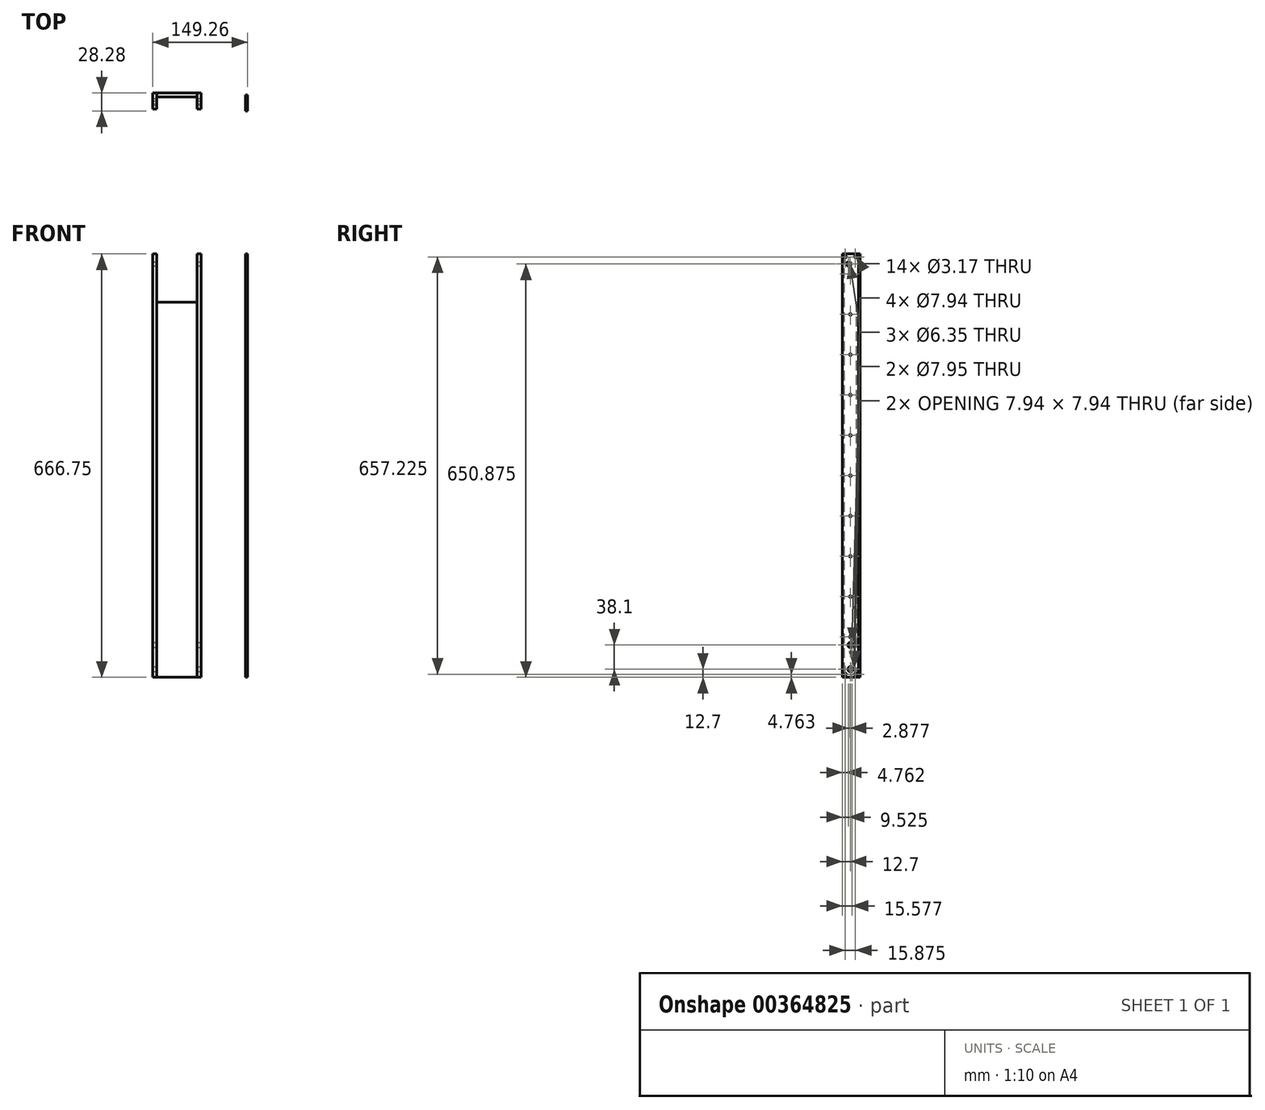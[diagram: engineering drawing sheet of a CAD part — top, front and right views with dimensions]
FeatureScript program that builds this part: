
annotation { "Feature Type Name" : "Feature", "Feature Type Description" : "" }
export const myFeature = defineFeature(function(context is Context, id is Id, definition is map)
    precondition{}
    {
        {
            var Q0;
            Q0=qCreatedBy(makeId("Top.planeOp"),FACE);
            var sketch = newSketch(context, id + "F0", { "sketchPlane" : qUnion([Q0])});
            skLineSegment(sketch, "E0", {"start": v(-38.1, -22.52) * mm, "end": v(-38.1, 2.88) * mm});
            skLineSegment(sketch, "E1", {"start": v(-38.1, 2.88) * mm, "end": v(38.1, 2.88) * mm});
            skLineSegment(sketch, "E2", {"start": v(38.1, 2.88) * mm, "end": v(38.1, -22.52) * mm});
            skLineSegment(sketch, "E3", {"start": v(38.1, -22.52) * mm, "end": v(31.75, -22.52) * mm});
            skLineSegment(sketch, "E4", {"start": v(31.75, -22.52) * mm, "end": v(31.75, -3.47) * mm});
            skLineSegment(sketch, "E5", {"start": v(31.75, -3.47) * mm, "end": v(-31.75, -3.47) * mm});
            skLineSegment(sketch, "E6", {"start": v(-31.75, -3.47) * mm, "end": v(-31.75, -22.52) * mm});
            skLineSegment(sketch, "E7", {"start": v(-31.75, -22.52) * mm, "end": v(-38.1, -22.52) * mm});
            skSolve(sketch);
        }
        {
            var Q0;
            Q0 = qSketchRegion(id + "F0", true);
            extrude(context, id + "F1", {"entities" : qUnion([Q0]), "depth" : 666.75 * mm, "offsetDistance" : 25.4 * mm});
        }
        {
            var Q0;
            Q0=makeQuery(id+"F1.opExtrude","SWEPT_FACE",FACE,{"disambiguationData":[OSD([sQuery(id+"F0.wireOp",EDGE,"E2")])]});
            var sketch = newSketch(context, id + "F2", { "sketchPlane" : qUnion([Q0])});
            skLineSegment(sketch, "E8", {"start": v(-9.82, -6.95) * mm, "end": v(-9.82, 63.87) * mm, "construction": true});
            skPoint(sketch, "E8.startSnap0", {"position": v(-9.82, 0) * mm});
            skCircle(sketch, "E9", {"center": v(-9.82, 12.7) * mm, "radius": 3.97 * mm});
            skCircle(sketch, "E10", {"center": v(-9.82, 50.8) * mm, "radius": 3.97 * mm});
            skSolve(sketch);
        }
        {
            var Q0;
            Q0 = qSketchRegion(id + "F2", true);
            var Q1;
            Q1=makeQuery(id+"F1.opExtrude","SWEPT_FACE",FACE,{"disambiguationData":[OSD([sQuery(id+"F0.wireOp",EDGE,"E0")])]});
            extrude(context, id + "F3", {"entities" : qUnion([Q0]), "operationType" : NewBodyOperationType.REMOVE, "endBound" : BoundingType.UP_TO_SURFACE, "oppositeDirection" : true, "depth" : 25.4 * mm, "endBoundEntityFace" : qUnion([Q1]), "offsetDistance" : 25.4 * mm});
        }
        {
            var Q0;
            Q0=makeQuery(id+"F1.opExtrude","SWEPT_FACE",FACE,{"disambiguationData":[OSD([sQuery(id+"F0.wireOp",EDGE,"E2")])]});
            var sketch = newSketch(context, id + "F4", { "sketchPlane" : qUnion([Q0])});
            skLineSegment(sketch, "E11", {"start": v(-13, 687.6) * mm, "end": v(-13, 625.88) * mm, "construction": true});
            skLineSegment(sketch, "E12", {"start": v(-33.47, 650.88) * mm, "end": v(-13, 650.88) * mm, "construction": true});
            skCircle(sketch, "E13", {"center": v(-13, 650.88) * mm, "radius": 3.18 * mm});
            skSolve(sketch);
        }
        {
            var Q0;
            Q0 = qSketchRegion(id + "F4", true);
            var Q1;
            Q1=makeQuery(id+"F1.opExtrude","SWEPT_FACE",FACE,{"disambiguationData":[OSD([sQuery(id+"F0.wireOp",EDGE,"E0")])]});
            extrude(context, id + "F5", {"entities" : qUnion([Q0]), "operationType" : NewBodyOperationType.REMOVE, "endBound" : BoundingType.UP_TO_SURFACE, "oppositeDirection" : true, "depth" : 25.4 * mm, "endBoundEntityFace" : qUnion([Q1]), "offsetDistance" : 25.4 * mm});
        }
        {
            var Q0;
            Q0=makeQuery(id+"F1.opExtrude","SWEPT_FACE",FACE,{"disambiguationData":[OSD([sQuery(id+"F0.wireOp",EDGE,"E1")])]});
            var sketch = newSketch(context, id + "F6", { "sketchPlane" : qUnion([Q0])});
            skLineSegment(sketch, "E14.bottom", {"start": v(-31.75, 666.75) * mm, "end": v(31.75, 666.75) * mm});
            skLineSegment(sketch, "E14.top", {"start": v(-31.75, 590.55) * mm, "end": v(31.75, 590.55) * mm});
            skLineSegment(sketch, "E14.left", {"start": v(-31.75, 666.75) * mm, "end": v(-31.75, 590.55) * mm});
            skLineSegment(sketch, "E14.right", {"start": v(31.75, 666.75) * mm, "end": v(31.75, 590.55) * mm});
            skSolve(sketch);
        }
        {
            var Q0;
            Q0 = qSketchRegion(id + "F6", true);
            var Q1;
            Q1=makeQuery(id+"F1.opExtrude","SWEPT_FACE",FACE,{"disambiguationData":[OSD([sQuery(id+"F0.wireOp",EDGE,"E5")])]});
            extrude(context, id + "F7", {"entities" : qUnion([Q0]), "operationType" : NewBodyOperationType.REMOVE, "endBound" : BoundingType.UP_TO_SURFACE, "oppositeDirection" : true, "depth" : 25.4 * mm, "endBoundEntityFace" : qUnion([Q1]), "offsetDistance" : 25.4 * mm});
        }
        {
            var Q0;
            Q0=qCreatedBy(makeId("Front.planeOp"),FACE);
            var sketch = newSketch(context, id + "F8", { "sketchPlane" : qUnion([Q0])});
            skLineSegment(sketch, "E15.bottom", {"start": v(107.99, 666.75) * mm, "end": v(111.16, 666.75) * mm});
            skLineSegment(sketch, "E15.top", {"start": v(107.99, 0) * mm, "end": v(111.16, 0) * mm});
            skLineSegment(sketch, "E15.left", {"start": v(107.99, 666.75) * mm, "end": v(107.99, 0) * mm});
            skLineSegment(sketch, "E15.right", {"start": v(111.16, 666.75) * mm, "end": v(111.16, 0) * mm});
            skSolve(sketch);
        }
        {
            var Q0;
            Q0 = qSketchRegion(id + "F8", true);
            extrude(context, id + "F9", {"entities" : qUnion([Q0]), "depth" : 25.4 * mm, "offsetDistance" : 25.4 * mm});
        }
        {
            var Q0;
            Q0=makeQuery(id+"F9.opExtrude","SWEPT_FACE",FACE,{"disambiguationData":[OSD([sQuery(id+"F8.wireOp",EDGE,"E15.right")])]});
            var sketch = newSketch(context, id + "F10", { "sketchPlane" : qUnion([Q0])});
            skLineSegment(sketch, "E16", {"start": v(-12.7, -6) * mm, "end": v(-12.7, 75.2) * mm, "construction": true});
            skPoint(sketch, "E16.startSnap0", {"position": v(-12.7, 0) * mm});
            skCircle(sketch, "E17", {"center": v(-12.7, 12.7) * mm, "radius": 3.98 * mm});
            skCircle(sketch, "E18", {"center": v(-12.7, 50.8) * mm, "radius": 3.98 * mm});
            skSolve(sketch);
        }
        {
            var Q0;
            Q0 = qSketchRegion(id + "F10", true);
            extrude(context, id + "F11", {"entities" : qUnion([Q0]), "operationType" : NewBodyOperationType.REMOVE, "oppositeDirection" : true, "depth" : 25.4 * mm, "offsetDistance" : 25.4 * mm});
        }
        {
            var Q0;
            Q0=makeQuery(id+"F9.opExtrude","SWEPT_FACE",FACE,{"disambiguationData":[OSD([sQuery(id+"F8.wireOp",EDGE,"E15.right")])]});
            var sketch = newSketch(context, id + "F12", { "sketchPlane" : qUnion([Q0])});
            skPoint(sketch, "E19.startSnap0", {"position": v(-12.7, 666.75) * mm});
            skLineSegment(sketch, "E20", {"start": v(-15.88, 665.84) * mm, "end": v(-15.87, 617.46) * mm, "construction": true});
            skCircle(sketch, "E21", {"center": v(-15.88, 650.88) * mm, "radius": 3.18 * mm});
            skSolve(sketch);
        }
        {
            var Q0;
            Q0 = qSketchRegion(id + "F12", true);
            extrude(context, id + "F13", {"entities" : qUnion([Q0]), "operationType" : NewBodyOperationType.REMOVE, "oppositeDirection" : true, "depth" : 25.4 * mm, "offsetDistance" : 25.4 * mm});
        }
        {
            var Q0;
            Q0=makeQuery(id+"F9.opExtrude","SWEPT_FACE",FACE,{"disambiguationData":[OSD([sQuery(id+"F8.wireOp",EDGE,"E15.right")])]});
            var sketch = newSketch(context, id + "F14", { "sketchPlane" : qUnion([Q0])});
            skLineSegment(sketch, "E22", {"start": v(-25.7, 661.99) * mm, "end": v(0.12, 661.99) * mm, "construction": true});
            skLineSegment(sketch, "E23", {"start": v(-20.64, 668.24) * mm, "end": v(-20.64, 653.73) * mm, "construction": true});
            skLineSegment(sketch, "E24", {"start": v(-4.76, 668.09) * mm, "end": v(-4.76, 653.73) * mm, "construction": true});
            skLineSegment(sketch, "E25", {"start": v(-24.96, 4.76) * mm, "end": v(-0.34, 4.76) * mm, "construction": true});
            skLineSegment(sketch, "E26", {"start": v(-20.64, -4.73) * mm, "end": v(-20.64, 22.19) * mm, "construction": true});
            skLineSegment(sketch, "E27", {"start": v(-4.76, -4.56) * mm, "end": v(-4.76, 21.67) * mm, "construction": true});
            skCircle(sketch, "E28", {"center": v(-20.64, 4.76) * mm, "radius": 1.59 * mm});
            skCircle(sketch, "E29", {"center": v(-4.76, 4.76) * mm, "radius": 1.59 * mm});
            skCircle(sketch, "E30", {"center": v(-4.76, 661.99) * mm, "radius": 1.59 * mm});
            skCircle(sketch, "E31", {"center": v(-20.64, 661.99) * mm, "radius": 1.59 * mm});
            skSolve(sketch);
        }
        {
            var Q0;
            Q0 = qSketchRegion(id + "F14", true);
            extrude(context, id + "F15", {"entities" : qUnion([Q0]), "operationType" : NewBodyOperationType.REMOVE, "oppositeDirection" : true, "depth" : 25.4 * mm, "offsetDistance" : 25.4 * mm});
        }
        {
            var Q0;
            Q0=makeQuery(id+"F9.opExtrude","SWEPT_FACE",FACE,{"disambiguationData":[OSD([sQuery(id+"F8.wireOp",EDGE,"E15.right")])]});
            var sketch = newSketch(context, id + "F16", { "sketchPlane" : qUnion([Q0])});
            skLineSegment(sketch, "E32", {"start": v(-12.7, 681.75) * mm, "end": v(-12.7, -17.36) * mm, "construction": true});
            skPoint(sketch, "E32.startSnap0", {"position": v(-12.7, 666.75) * mm});
            skLineSegment(sketch, "E33", {"start": v(-23.35, 65.71) * mm, "end": v(-3.6, 65.71) * mm, "construction": true});
            skLineSegment(sketch, "E34", {"start": v(-25.4, 153.33) * mm, "end": v(-3.6, 153.33) * mm, "construction": true});
            skLineSegment(sketch, "E35", {"start": v(-20.66, 269.36) * mm, "end": v(-3.6, 269.36) * mm, "construction": true});
            skLineSegment(sketch, "E36", {"start": v(-25.4, 636.3) * mm, "end": v(-7.3, 636.3) * mm, "construction": true});
            skCircle(sketch, "E37", {"center": v(-12.7, 63.5) * mm, "radius": 1.59 * mm});
            skCircle(sketch, "E38", {"center": v(-12.7, 127) * mm, "radius": 1.59 * mm});
            skCircle(sketch, "E39", {"center": v(-12.7, 190.5) * mm, "radius": 1.59 * mm});
            skCircle(sketch, "E40", {"center": v(-12.7, 254) * mm, "radius": 1.59 * mm});
            skCircle(sketch, "E41", {"center": v(-12.7, 317.5) * mm, "radius": 1.59 * mm});
            skCircle(sketch, "E42", {"center": v(-12.7, 381) * mm, "radius": 1.59 * mm});
            skCircle(sketch, "E43", {"center": v(-12.7, 444.5) * mm, "radius": 1.59 * mm});
            skCircle(sketch, "E44", {"center": v(-12.7, 508) * mm, "radius": 1.59 * mm});
            skCircle(sketch, "E45", {"center": v(-12.7, 571.5) * mm, "radius": 1.59 * mm});
            skCircle(sketch, "E46", {"center": v(-12.7, 635) * mm, "radius": 1.59 * mm});
            skSolve(sketch);
        }
        {
            var Q0;
            Q0 = qSketchRegion(id + "F16", true);
            extrude(context, id + "F17", {"entities" : qUnion([Q0]), "operationType" : NewBodyOperationType.REMOVE, "oppositeDirection" : true, "depth" : 25.4 * mm, "offsetDistance" : 25.4 * mm});
        }
    });
